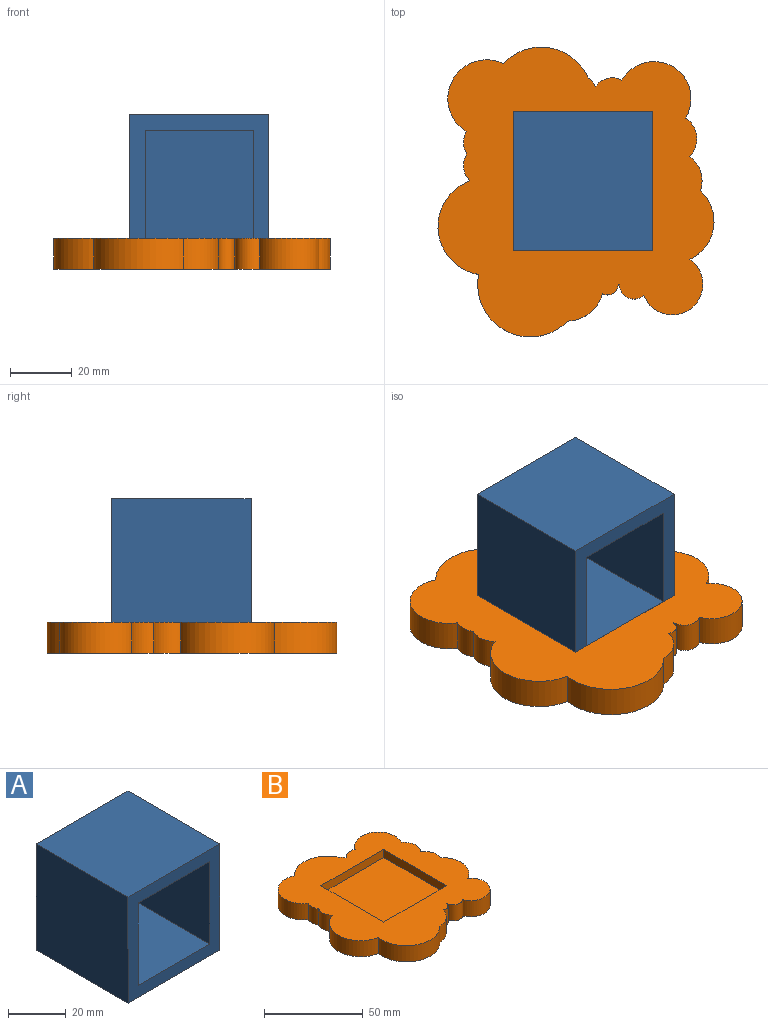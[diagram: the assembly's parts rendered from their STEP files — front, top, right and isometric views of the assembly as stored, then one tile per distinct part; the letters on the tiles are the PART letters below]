
ASSEMBLY  parts=2 mates=1
PART A: 11 faces, bbox 45x45x45 mm
  f0: plane 45x45mm, normal (0,-1,0), area 800mm2, adj f1,f2,f3,f4,f6,f7,f8,f9
  f1: plane 45x45mm, normal (-1,0,0), area 2025mm2, adj f0,f2,f4,f5
  f2: plane 45x45mm, normal (0,0,-1), area 2025mm2, adj f0,f1,f3,f5
  f3: plane 45x45mm, normal (1,0,0), area 2025mm2, adj f0,f2,f4,f5
  f4: plane 45x45mm, normal (0,0,1), area 2025mm2, adj f0,f1,f3,f5
  f5: plane 45x45mm, normal (0,1,0), area 2025mm2, adj f1,f2,f3,f4
  f6: plane 40x35mm, normal (0,0,-1), area 1400mm2, adj f0,f7,f9,f10
  f7: plane 40x35mm, normal (1,0,0), area 1400mm2, adj f0,f6,f8,f10
  f8: plane 40x35mm, normal (0,0,1), area 1400mm2, adj f0,f7,f9,f10
  f9: plane 40x35mm, normal (-1,0,0), area 1400mm2, adj f0,f6,f8,f10
  f10: plane 35x35mm, normal (0,-1,0), area 1225mm2, adj f6,f7,f8,f9
PART B: 24 faces, bbox 89.2x93.6x10 mm
  f0: plane 93.6x89.16mm, normal (0,0,1), area 4320.4mm2, adj f1,f2,f3,f4,f5,f6,f7,f8
  f1: cylinder r=7.43mm len=10mm, axis (0,0,-1), area 94.3mm2, adj f0,f2,f17,f18
  f2: cylinder r=15.7mm len=30.22mm, axis (0,0,-1), area 411.8mm2, adj f0,f1,f3,f18
  f3: cylinder r=16.96mm len=29.09mm, axis (0,0,-1), area 433.7mm2, adj f0,f2,f4,f18
  f4: cylinder r=11.86mm len=11.21mm, axis (0,0,-1), area 153.3mm2, adj f0,f3,f5,f18
  f5: cylinder r=3.43mm len=10mm, axis (0,0,-1), area 71.3mm2, adj f0,f4,f6,f18
  f6: plane 10x0.36mm, normal (0,-1,0), area 3.6mm2, adj f0,f5,f7,f18
  f7: cylinder r=4.75mm len=10mm, axis (0,0,-1), area 109.4mm2, adj f0,f6,f8,f18
  f8: cylinder r=9.86mm len=19.06mm, axis (0,0,-1), area 368.4mm2, adj f0,f7,f9,f18
  f9: cylinder r=13.45mm len=22.17mm, axis (0,0,-1), area 265.2mm2, adj f0,f8,f10,f18
  f10: cylinder r=9.59mm len=11.07mm, axis (0,0,-1), area 125mm2, adj f0,f9,f11,f18
  f11: cylinder r=7.91mm len=12.39mm, axis (0,0,-1), area 143.3mm2, adj f0,f10,f12,f18
  f12: cylinder r=11.96mm len=22.31mm, axis (0,0,-1), area 379.1mm2, adj f0,f11,f13,f18
  f13: cylinder r=6.72mm len=10mm, axis (0,0,-1), area 95.6mm2, adj f0,f12,f14,f18
  f14: cylinder r=8.38mm len=10mm, axis (0,0,-1), area 36.3mm2, adj f0,f13,f15,f18
  f15: cylinder r=16.64mm len=27.49mm, axis (0,0,-1), area 330.5mm2, adj f0,f14,f16,f18
  f16: cylinder r=12.52mm len=23.16mm, axis (0,0,-1), area 379.9mm2, adj f0,f15,f17,f18
  f17: cylinder r=7.44mm len=10mm, axis (0,0,-1), area 75.2mm2, adj f0,f1,f16,f18
  f18: plane 93.6x89.16mm, normal (0,0,-1), area 6345.4mm2, adj f1,f2,f3,f4,f5,f6,f7,f8
  f19: plane 45x5mm, normal (0,1,0), area 225mm2, adj f0,f20,f22,f23
  f20: plane 45x5mm, normal (-1,0,0), area 225mm2, adj f0,f19,f21,f23
  f21: plane 45x5mm, normal (0,-1,0), area 225mm2, adj f0,f20,f22,f23
  f22: plane 45x5mm, normal (1,0,0), area 225mm2, adj f0,f19,f21,f23
  f23: plane 45x45mm, normal (0,0,1), area 2025mm2, adj f19,f20,f21,f22
PLACE A t=(59.68,62.24,-39.07)mm
PLACE B t=(50.97,6.45,-44.07)mm
MATE fastened B.f23 <-> A.f2  axis (0,0,1) through (82.18,39.74,-39.07)mm
